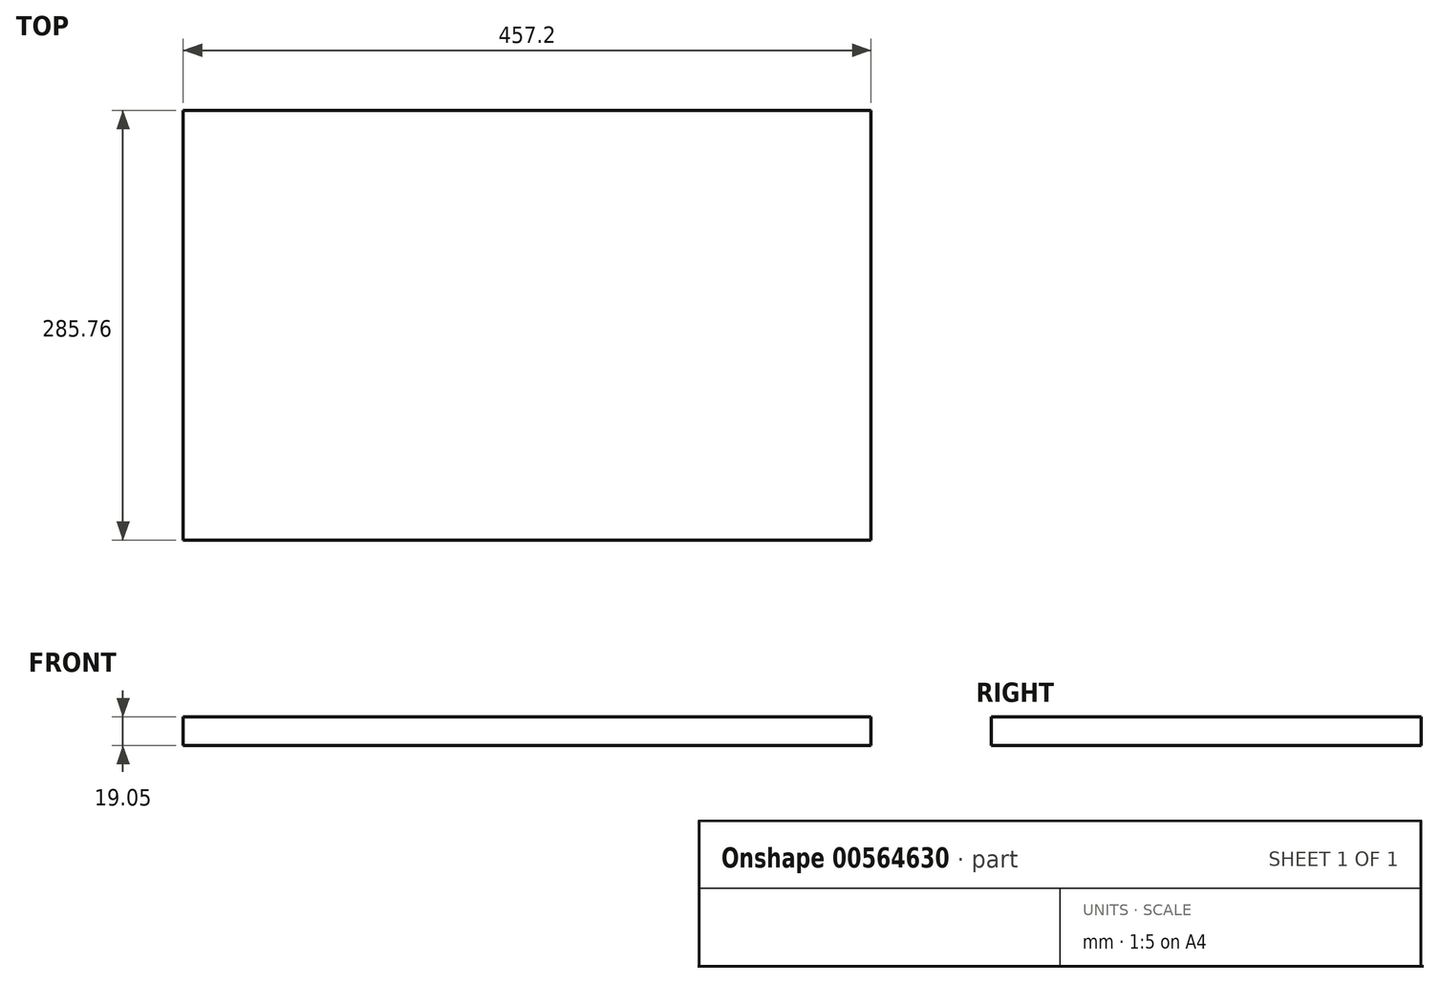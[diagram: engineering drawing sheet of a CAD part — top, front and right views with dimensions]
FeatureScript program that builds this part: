
annotation { "Feature Type Name" : "Feature", "Feature Type Description" : "" }
export const myFeature = defineFeature(function(context is Context, id is Id, definition is map)
    precondition{}
    {
        {
            var Q0;
            Q0=qCreatedBy(makeId("Top.planeOp"),FACE);
            var sketch = newSketch(context, id + "F0", { "sketchPlane" : qUnion([Q0])});
            skLineSegment(sketch, "E0.bottom", {"start": v(-228.6, 142.88) * mm, "end": v(228.6, 142.88) * mm});
            skLineSegment(sketch, "E0.top", {"start": v(-228.6, -142.88) * mm, "end": v(228.6, -142.88) * mm});
            skLineSegment(sketch, "E0.left", {"start": v(-228.6, 142.88) * mm, "end": v(-228.6, -142.87) * mm});
            skLineSegment(sketch, "E0.right", {"start": v(228.6, 142.88) * mm, "end": v(228.6, -142.87) * mm});
            skPoint(sketch, "E0.middle", {"position": v(0, 0) * mm});
            skSolve(sketch);
        }
        {
            var Q0;
            Q0=makeQuery(id+"F0.imprint","IMPRINT",FACE,{"disambiguationData":[TD([[makeQuery(id+"F0.imprint","IMPRINT",EDGE,{"derivedFrom":sQuery(id+"F0.wireOp",EDGE,"E0.bottom")}),-1.0]])]});
            extrude(context, id + "F1", {"entities" : qUnion([Q0]), "depth" : 19.05 * mm, "offsetDistance" : 25.4 * mm});
        }
    });
